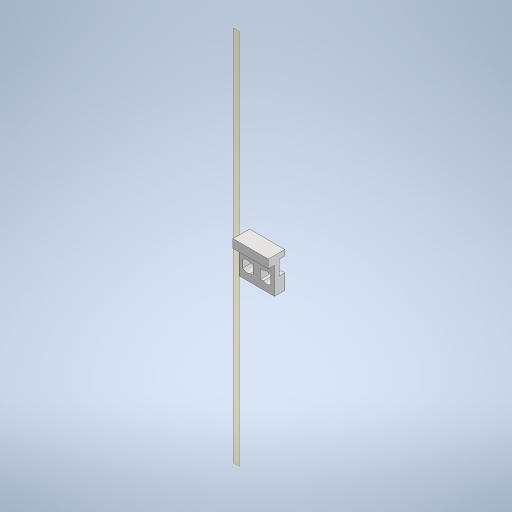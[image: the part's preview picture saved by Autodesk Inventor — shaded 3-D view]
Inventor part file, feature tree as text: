
AUTODESK INVENTOR PART (.ipt)
format: ipt  version: 2023 (Build 270158000, 158)  size: 589,824 bytes
history: native  units: mm
features: reference x29, extrude x10, other x9, sketch x4, plane x2
ambient origin geometry x8: Origin, YZ Plane, XZ Plane, XY Plane, X Axis, Y Axis, Z Axis, Center Point
bodies: Body1 (feature_tree)
feature tree (54):
  plane  "Work Plane1"
  sketch  "Sketch2"  dims[d14=22.0mm d15=14.0mm]
  extrude  "Extrusion3"  Depth=14.0mm
  extrude  "Extrusion4"  Depth=0.1mm
  extrude  "Extrusion7"  Depth=1.0mm
  plane  "Work Plane2"
  sketch  "Sketch14"  dims[d18=0.1mm d19=1.0mm]
  extrude  "Extrusion12"  Depth=2.0mm
  extrude  "Extrusion13"  Depth=10.0mm
  extrude  "Extrusion14"  Depth=28.25mm TaperAngle=0.0deg
  extrude  "Extrusion15"  Depth=11.0mm TaperAngle=0.0deg
  sketch  "Sketch16"  dims[d20=2.0mm d21=2.0mm d22=0.15mm d24=28.25mm d25=0.0mm d26=11.0mm d27=0.0mm d32=480.5mm d33=0.0mm d65=0.15mm d66=0.15mm d67=2.0mm d68=15.0mm d69=0.15mm d70=0.15mm d71=0.15mm d72=0.15mm d73=13.7mm d74=0.0mm d75=11.4mm d76=0.0mm d77=12.05mm d78=0.0mm d79=10.4mm d80=0.0mm d81=5.0mm d82=0.0mm d88=1.0mm d90=1.0mm d91=0.75mm d92=1.0mm d93=0.15mm d94=1.0mm d95=13.7mm d96=0.0mm d97=12.3mm d98=0.0mm d99=10.0mm d103=5.5mm]
  extrude  "Extrusion17"  Depth=10.0mm TaperAngle=0.0deg
  extrude  "Extrusion18"  Depth=10.0mm
  extrude  "Extrusion16"  Depth=10.0mm
  reference  "Reference4"
  reference  "Reference5"
  reference  "Reference6"
  reference  "Reference7"
  reference  "Reference8"
  reference  "Reference9"
  reference  "Reference10"
  reference  "Reference14"
  reference  "Reference15"
  reference  "Reference16"
  reference  "Reference17"
  reference  "Reference18"
  reference  "Reference19"
  reference  "Reference20"
  reference  "Reference21"
  reference  "Reference22"
  reference  "Reference23"
  reference  "Reference24"
  reference  "Reference25"
  reference  "Reference26"
  reference  "Reference27"
  reference  "Reference28"
  sketch  "Sketch6"  dims[d16=0.15mm d17=0.1mm]
  reference  "Reference33"
  reference  "Reference34"
  reference  "Reference56"
  reference  "Reference125"
  reference  "Reference126"
  reference  "Reference127"
  reference  "Reference128"
  parser-record x1  (decoder bookkeeping rows leaked as tree rows — omitted from the tree; the rows remain in map.json)
  other  "Assembly_V7.iam"
  other  "rack_V7:1"
  other  "motor:2"
  other  "motor:1"
  other  "pinion_V7:1"
  other  "pinion_V7:2"
  other  "moulding:1"
  other  "ESP-12F:1"
note: 1 file-system path scrubbed to <path> (originals preserved in map.json)
